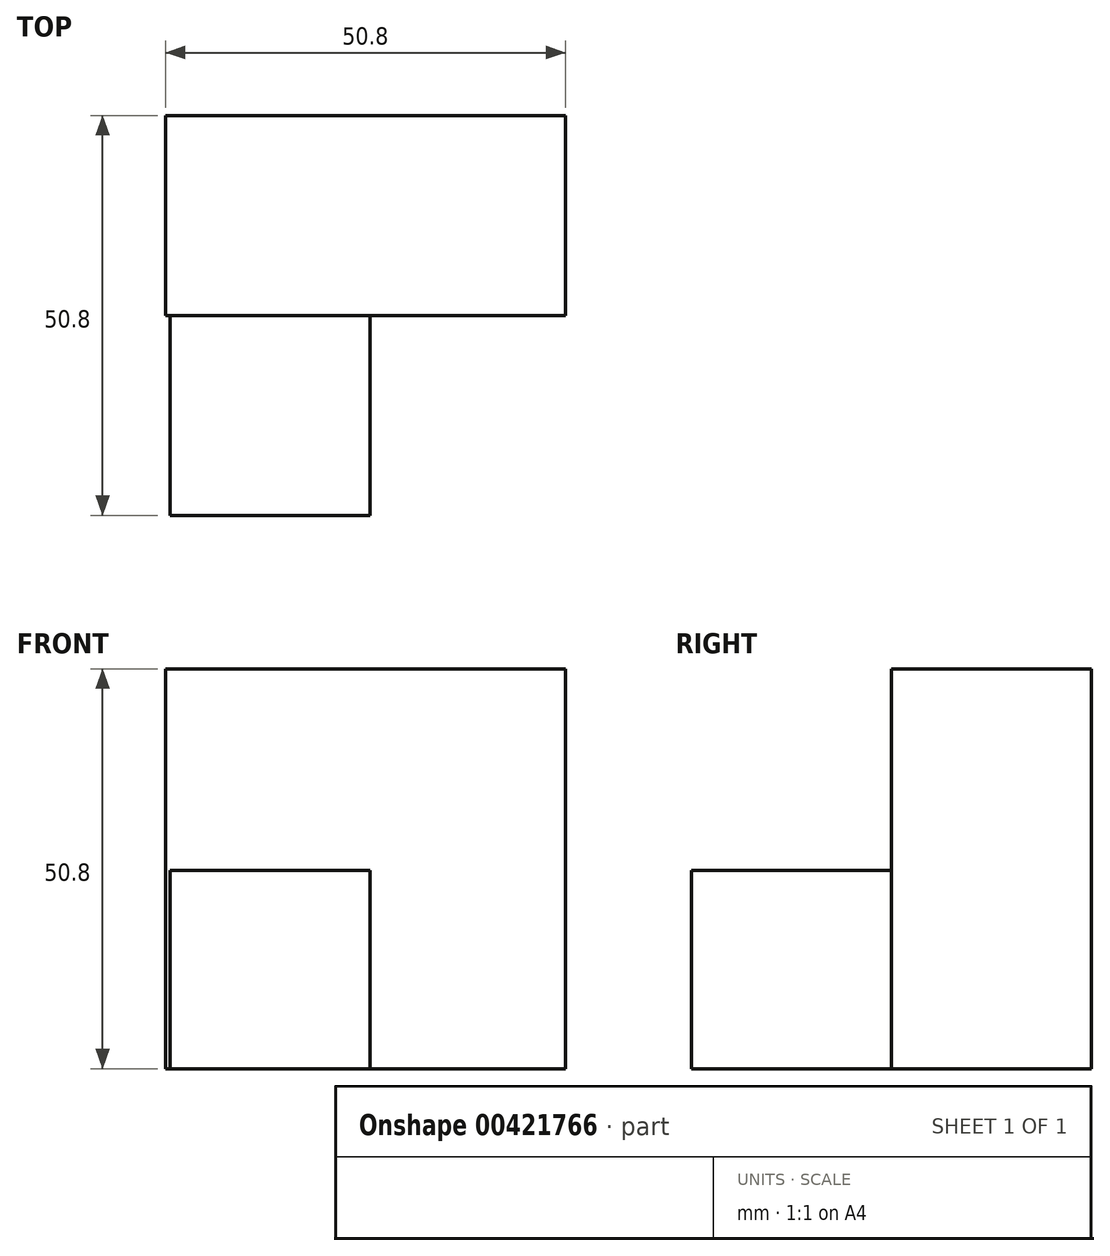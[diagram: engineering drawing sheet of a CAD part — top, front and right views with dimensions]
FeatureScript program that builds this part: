
annotation { "Feature Type Name" : "Feature", "Feature Type Description" : "" }
export const myFeature = defineFeature(function(context is Context, id is Id, definition is map)
    precondition{}
    {
        {
            var Q0;
            Q0=qCreatedBy(makeId("Front.planeOp"),FACE);
            var sketch = newSketch(context, id + "F0", { "sketchPlane" : qUnion([Q0])});
            skLineSegment(sketch, "E0.bottom", {"start": v(-22.92, 42.02) * mm, "end": v(27.88, 42.02) * mm});
            skLineSegment(sketch, "E0.top", {"start": v(-22.92, -8.78) * mm, "end": v(27.88, -8.78) * mm});
            skLineSegment(sketch, "E0.left", {"start": v(-22.92, 42.02) * mm, "end": v(-22.92, -8.78) * mm});
            skLineSegment(sketch, "E0.right", {"start": v(27.88, 42.02) * mm, "end": v(27.88, -8.78) * mm});
            skSolve(sketch);
        }
        {
            var Q0;
            Q0=makeQuery(id+"F0.imprint","IMPRINT",FACE,{"disambiguationData":[TD([[makeQuery(id+"F0.imprint","IMPRINT",EDGE,{"derivedFrom":sQuery(id+"F0.wireOp",EDGE,"E0.bottom")}),-1.0]])]});
            extrude(context, id + "F1", {"entities" : qUnion([Q0]), "depth" : 25.4 * mm});
        }
        {
            var Q0;
            Q0=qCreatedBy(makeId("Front.planeOp"),FACE);
            var sketch = newSketch(context, id + "F2", { "sketchPlane" : qUnion([Q0])});
            skLineSegment(sketch, "E1.bottom", {"start": v(-22.34, 16.42) * mm, "end": v(3.06, 16.42) * mm});
            skLineSegment(sketch, "E1.top", {"start": v(-22.34, -8.78) * mm, "end": v(3.06, -8.78) * mm});
            skLineSegment(sketch, "E1.left", {"start": v(-22.34, 16.42) * mm, "end": v(-22.34, -8.78) * mm});
            skLineSegment(sketch, "E1.right", {"start": v(3.06, 16.42) * mm, "end": v(3.06, -8.78) * mm});
            skSolve(sketch);
        }
        {
            var Q0;
            Q0 = qSketchRegion(id + "F2", true);
            extrude(context, id + "F3", {"entities" : qUnion([Q0]), "operationType" : NewBodyOperationType.ADD, "depth" : 50.8 * mm});
        }
    });
